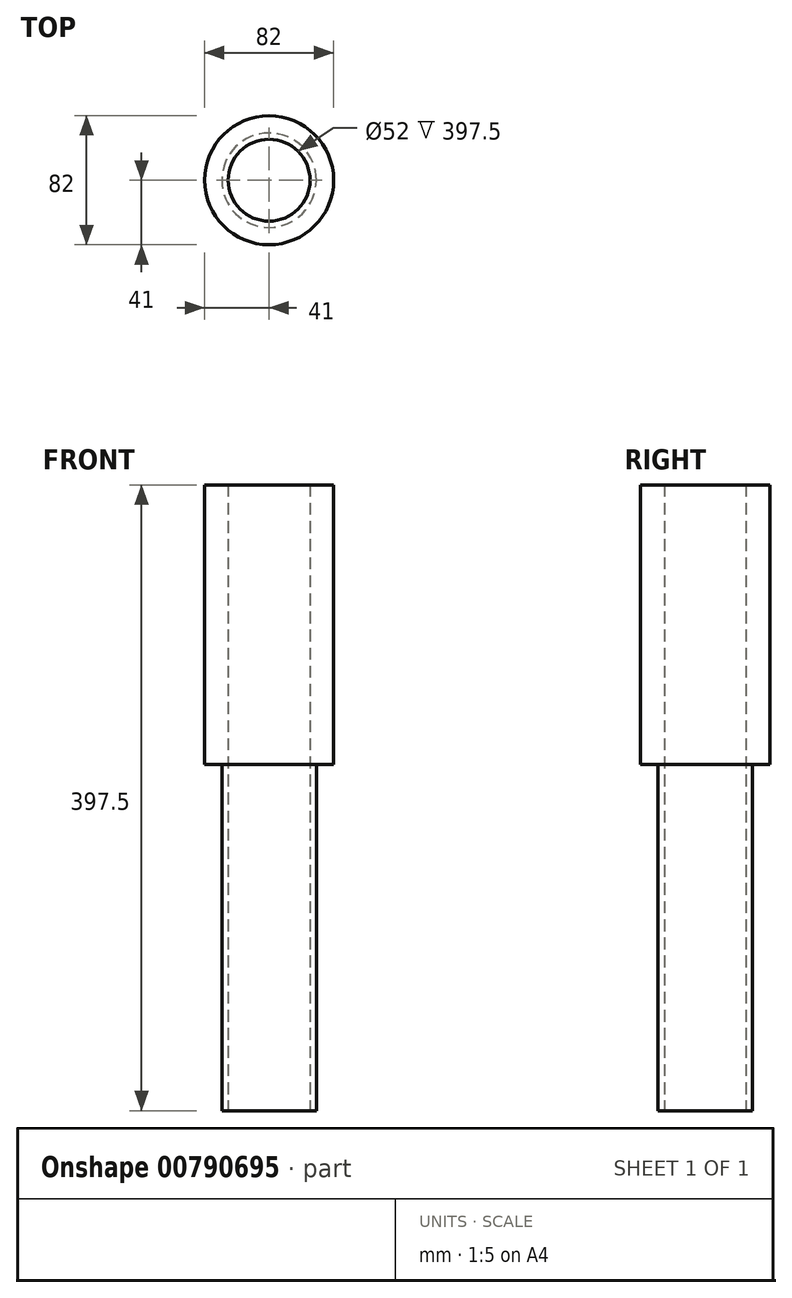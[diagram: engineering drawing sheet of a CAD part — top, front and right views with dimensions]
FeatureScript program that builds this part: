
annotation { "Feature Type Name" : "Feature", "Feature Type Description" : "" }
export const myFeature = defineFeature(function(context is Context, id is Id, definition is map)
    precondition{}
    {
        {
            var Q0;
            Q0=qCreatedBy(makeId("Top.planeOp"),FACE);
            var sketch = newSketch(context, id + "F0", { "sketchPlane" : qUnion([Q0])});
            skCircle(sketch, "E0", {"center": v(0, 0) * mm, "radius": 41 * mm});
            skCircle(sketch, "E1", {"center": v(0, 0) * mm, "radius": 26 * mm});
            skSolve(sketch);
        }
        {
            var Q0;
            Q0=makeQuery(id+"F0.imprint","IMPRINT",FACE,{"disambiguationData":[TD([[makeQuery(id+"F0.imprint","IMPRINT",EDGE,{"derivedFrom":sQuery(id+"F0.wireOp",EDGE,"E0")}),1.0]])]});
            extrude(context, id + "F1", {"entities" : qUnion([Q0]), "depth" : (180 - 2.5) * mm, "offsetDistance" : 25 * mm});
        }
        {
            var Q0;
            Q0=qCreatedBy(makeId("Top.planeOp"),FACE);
            var sketch = newSketch(context, id + "F2", { "sketchPlane" : qUnion([Q0])});
            skCircle(sketch, "E2", {"center": v(0, 0) * mm, "radius": 30 * mm});
            skCircle(sketch, "E3", {"center": v(0, 0) * mm, "radius": 26 * mm});
            skSolve(sketch);
        }
        {
            var Q0;
            Q0=makeQuery(id+"F2.imprint","IMPRINT",FACE,{"disambiguationData":[TD([[makeQuery(id+"F2.imprint","IMPRINT",EDGE,{"derivedFrom":sQuery(id+"F2.wireOp",EDGE,"E2")}),1.0]])]});
            extrude(context, id + "F3", {"entities" : qUnion([Q0]), "operationType" : NewBodyOperationType.ADD, "oppositeDirection" : true, "depth" : 220 * mm, "offsetDistance" : 25 * mm});
        }
    });
